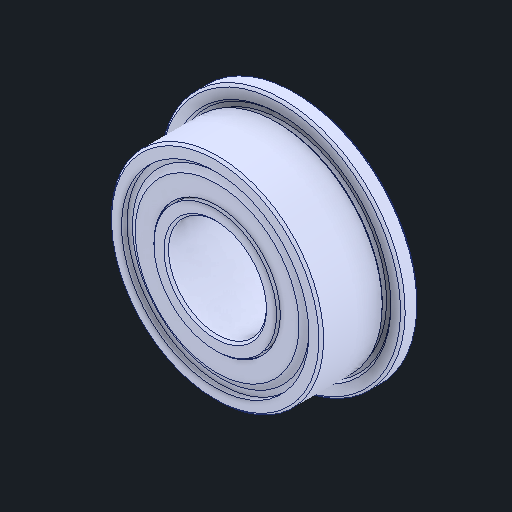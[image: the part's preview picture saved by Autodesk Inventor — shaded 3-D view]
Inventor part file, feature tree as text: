
AUTODESK INVENTOR PART (.ipt)
format: ipt  version: 2025 (Build 290162000, 162)  size: 637,952 bytes
history: native  units: mm
features: other x12, revolve x3
ambient origin geometry x8: Origin, YZ Plane, XZ Plane, XY Plane, X Axis, Y Axis, Z Axis, Center Point
bodies: 实体1 (feature_tree), 实体2 (feature_tree), 实体3 (feature_tree), 实体4 (feature_tree), 实体5 (feature_tree), 实体6 (feature_tree), 实体7 (feature_tree), 实体8 (feature_tree), 实体9 (feature_tree), 实体10 (feature_tree), 实体11 (feature_tree), 实体12 (feature_tree), 实体13 (feature_tree), 实体14 (feature_tree), 实体15 (feature_tree)
feature tree (15):
  revolve  "Revolve3"  [1 undecoded]
  other  "CirPattern3[1]"
  other  "CirPattern3[2]"
  other  "CirPattern3[3]"
  other  "CirPattern3[4]"
  other  "CirPattern3[5]"
  other  "CirPattern3[6]"
  other  "CirPattern3[7]"
  other  "CirPattern3[8]"
  other  "CirPattern3[9]"
  other  "CirPattern3[10]"
  other  "Cut-Revolve1[1]"
  other  "Cut-Revolve1[2]"
  revolve  "Revolve4[1]"  [1 undecoded]
  revolve  "Revolve4[2]"  [1 undecoded]
note: 3 required parameter values undecoded (feature->parameter linkage not recoverable at this tier; creation-order binding heuristic only, values carry confidence <= 0.55)
